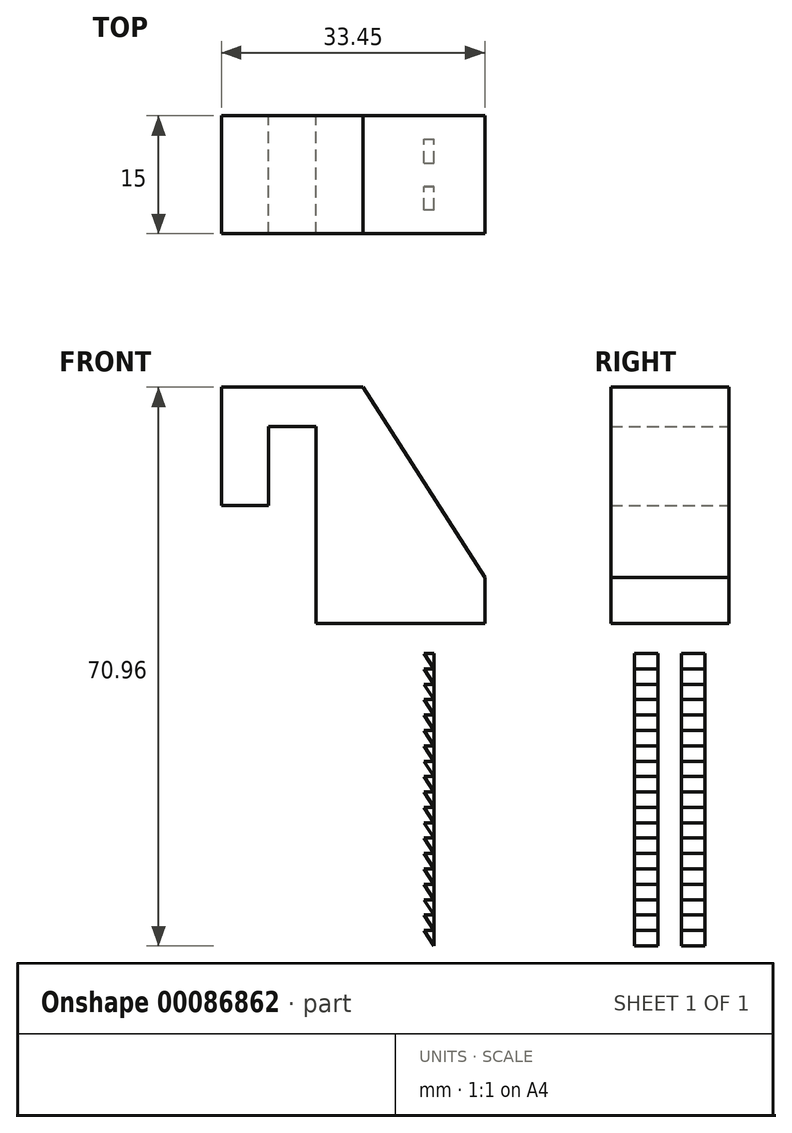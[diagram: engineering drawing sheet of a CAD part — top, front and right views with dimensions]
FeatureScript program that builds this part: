
annotation { "Feature Type Name" : "Feature", "Feature Type Description" : "" }
export const myFeature = defineFeature(function(context is Context, id is Id, definition is map)
    precondition{}
    {
        {
            var Q0;
            Q0=qCreatedBy(makeId("Front.planeOp"),FACE);
            var sketch = newSketch(context, id + "F0", { "sketchPlane" : qUnion([Q0])});
            skLineSegment(sketch, "E0.bottom", {"start": v(-22.95, -4.4) * mm, "end": v(-16.95, -4.4) * mm});
            skLineSegment(sketch, "E0.top", {"start": v(-22.95, 10.6) * mm, "end": v(-16.95, 10.6) * mm});
            skLineSegment(sketch, "E0.left", {"start": v(-22.95, -4.4) * mm, "end": v(-22.95, 10.6) * mm});
            skLineSegment(sketch, "E0.right", {"start": v(-16.95, -4.4) * mm, "end": v(-16.95, 10.6) * mm});
            skLineSegment(sketch, "E1.bottom", {"start": v(-16.95, 10.6) * mm, "end": v(-10.95, 10.6) * mm});
            skLineSegment(sketch, "E1.top", {"start": v(-16.95, 5.6) * mm, "end": v(-10.95, 5.6) * mm});
            skLineSegment(sketch, "E1.left", {"start": v(-16.95, 10.6) * mm, "end": v(-16.95, 5.6) * mm});
            skLineSegment(sketch, "E1.right", {"start": v(-10.95, 10.6) * mm, "end": v(-10.95, 5.6) * mm});
            skLineSegment(sketch, "E2.bottom", {"start": v(-10.95, 10.6) * mm, "end": v(-4.95, 10.6) * mm});
            skLineSegment(sketch, "E2.top", {"start": v(-10.95, -19.4) * mm, "end": v(-4.95, -19.4) * mm});
            skLineSegment(sketch, "E2.left", {"start": v(-10.95, 10.6) * mm, "end": v(-10.95, -19.4) * mm});
            skLineSegment(sketch, "E2.right", {"start": v(-4.95, 10.6) * mm, "end": v(-4.95, -19.4) * mm});
            skLineSegment(sketch, "E3.left", {"start": v(-4.95, -19.4) * mm, "end": v(-4.95, -13.53) * mm});
            skLineSegment(sketch, "E4.bottom", {"start": v(-4.95, -13.53) * mm, "end": v(10.5, -13.53) * mm});
            skLineSegment(sketch, "E4.top", {"start": v(-4.95, -19.4) * mm, "end": v(10.5, -19.4) * mm});
            skLineSegment(sketch, "E4.left", {"start": v(-4.95, -13.53) * mm, "end": v(-4.95, -19.4) * mm});
            skLineSegment(sketch, "E4.right", {"start": v(10.5, -13.53) * mm, "end": v(10.5, -19.4) * mm});
            skLineSegment(sketch, "E5.bottom", {"start": v(10.5, -19.4) * mm, "end": v(4.05, -19.4) * mm});
            skLineSegment(sketch, "E5.top", {"start": v(10.5, -70.16) * mm, "end": v(4.05, -70.16) * mm});
            skLineSegment(sketch, "E5.left", {"start": v(10.5, -19.4) * mm, "end": v(10.5, -70.16) * mm});
            skLineSegment(sketch, "E5.right", {"start": v(4.05, -19.4) * mm, "end": v(4.05, -70.16) * mm});
            skLineSegment(sketch, "E6", {"start": v(4.05, -23.23) * mm, "end": v(2.78, -23.23) * mm});
            skPoint(sketch, "E6.endSnap0", {"position": v(2.78, -19.4) * mm});
            skLineSegment(sketch, "E7", {"start": v(2.78, -23.23) * mm, "end": v(4.05, -25.18) * mm});
            skLineSegment(sketch, "E8", {"start": v(4.05, -25.17) * mm, "end": v(2.78, -25.17) * mm});
            skLineSegment(sketch, "E9", {"start": v(2.78, -25.17) * mm, "end": v(4.05, -27.13) * mm});
            skLineSegment(sketch, "E10", {"start": v(4.05, -27.13) * mm, "end": v(2.78, -27.13) * mm});
            skLineSegment(sketch, "E11", {"start": v(2.78, -27.13) * mm, "end": v(4.05, -29.08) * mm});
            skLineSegment(sketch, "E12", {"start": v(4.05, -29.08) * mm, "end": v(2.78, -29.08) * mm});
            skLineSegment(sketch, "E13", {"start": v(2.78, -29.08) * mm, "end": v(4.05, -31.04) * mm});
            skLineSegment(sketch, "E14", {"start": v(4.05, -31.04) * mm, "end": v(2.78, -31.04) * mm});
            skLineSegment(sketch, "E15", {"start": v(2.78, -31.04) * mm, "end": v(4.05, -33) * mm});
            skLineSegment(sketch, "E16", {"start": v(4.05, -33) * mm, "end": v(2.78, -33) * mm});
            skLineSegment(sketch, "E17", {"start": v(2.78, -33) * mm, "end": v(4.05, -34.95) * mm});
            skLineSegment(sketch, "E18", {"start": v(4.05, -34.95) * mm, "end": v(2.78, -34.95) * mm});
            skLineSegment(sketch, "E19", {"start": v(2.78, -34.95) * mm, "end": v(4.05, -36.9) * mm});
            skLineSegment(sketch, "E20", {"start": v(4.05, -36.9) * mm, "end": v(2.78, -36.9) * mm});
            skLineSegment(sketch, "E21", {"start": v(2.78, -36.9) * mm, "end": v(4.05, -38.86) * mm});
            skLineSegment(sketch, "E22", {"start": v(4.05, -38.86) * mm, "end": v(2.78, -38.86) * mm});
            skLineSegment(sketch, "E23", {"start": v(2.78, -38.86) * mm, "end": v(4.05, -40.81) * mm});
            skLineSegment(sketch, "E24", {"start": v(4.05, -40.81) * mm, "end": v(2.78, -40.81) * mm});
            skLineSegment(sketch, "E25", {"start": v(2.78, -40.81) * mm, "end": v(4.05, -42.77) * mm});
            skLineSegment(sketch, "E26", {"start": v(4.05, -42.77) * mm, "end": v(2.78, -42.77) * mm});
            skLineSegment(sketch, "E27", {"start": v(2.78, -42.77) * mm, "end": v(4.05, -44.72) * mm});
            skLineSegment(sketch, "E28", {"start": v(4.05, -44.72) * mm, "end": v(2.78, -44.72) * mm});
            skLineSegment(sketch, "E29", {"start": v(2.78, -44.72) * mm, "end": v(4.05, -46.67) * mm});
            skLineSegment(sketch, "E30", {"start": v(4.05, -46.67) * mm, "end": v(2.78, -46.67) * mm});
            skLineSegment(sketch, "E31", {"start": v(2.78, -46.67) * mm, "end": v(4.05, -48.63) * mm});
            skLineSegment(sketch, "E32", {"start": v(4.05, -48.63) * mm, "end": v(2.78, -48.63) * mm});
            skLineSegment(sketch, "E33", {"start": v(2.78, -48.63) * mm, "end": v(4.05, -50.58) * mm});
            skLineSegment(sketch, "E34", {"start": v(4.05, -50.58) * mm, "end": v(2.78, -50.58) * mm});
            skLineSegment(sketch, "E35", {"start": v(2.78, -50.58) * mm, "end": v(4.05, -52.54) * mm});
            skLineSegment(sketch, "E36", {"start": v(4.05, -52.54) * mm, "end": v(2.78, -52.54) * mm});
            skLineSegment(sketch, "E37", {"start": v(2.78, -52.54) * mm, "end": v(4.05, -54.5) * mm});
            skLineSegment(sketch, "E38", {"start": v(4.05, -54.5) * mm, "end": v(2.78, -54.5) * mm});
            skLineSegment(sketch, "E39", {"start": v(2.78, -54.5) * mm, "end": v(4.05, -56.45) * mm});
            skLineSegment(sketch, "E40", {"start": v(4.05, -56.45) * mm, "end": v(2.78, -56.45) * mm});
            skLineSegment(sketch, "E41", {"start": v(2.78, -56.45) * mm, "end": v(4.05, -58.4) * mm});
            skLineSegment(sketch, "E42", {"start": v(4.05, -58.4) * mm, "end": v(2.78, -58.4) * mm});
            skLineSegment(sketch, "E43", {"start": v(2.78, -58.4) * mm, "end": v(4.05, -60.36) * mm});
            skLineSegment(sketch, "E44", {"start": v(4.05, -60.36) * mm, "end": v(2.78, -60.36) * mm});
            skLineSegment(sketch, "E45", {"start": v(2.78, -60.36) * mm, "end": v(4.05, -62.31) * mm});
            skLineSegment(sketch, "E46", {"start": v(4.05, -62.31) * mm, "end": v(2.78, -62.31) * mm});
            skLineSegment(sketch, "E47", {"start": v(2.78, -62.31) * mm, "end": v(4.05, -64.27) * mm});
            skLineSegment(sketch, "E48", {"start": v(4.05, -64.27) * mm, "end": v(2.78, -64.27) * mm});
            skLineSegment(sketch, "E49", {"start": v(2.78, -64.27) * mm, "end": v(4.05, -66.22) * mm});
            skLineSegment(sketch, "E50", {"start": v(4.05, -66.22) * mm, "end": v(2.78, -66.22) * mm});
            skLineSegment(sketch, "E51", {"start": v(2.78, -66.22) * mm, "end": v(4.05, -68.18) * mm});
            skLineSegment(sketch, "E52", {"start": v(4.05, -68.18) * mm, "end": v(2.78, -68.18) * mm});
            skLineSegment(sketch, "E53", {"start": v(2.78, -68.18) * mm, "end": v(4.05, -70.13) * mm});
            skLineSegment(sketch, "E54", {"start": v(10.5, -13.53) * mm, "end": v(-4.95, 10.6) * mm});
            skLineSegment(sketch, "E55", {"start": v(10.5, -70.16) * mm, "end": v(4.05, -60.36) * mm});
            skLineSegment(sketch, "E56", {"start": v(9.74, -69) * mm, "end": v(10.5, -69) * mm});
            skSolve(sketch);
        }
        {
            var Q0;
            Q0=makeQuery(id+"F0.imprint","IMPRINT",FACE,{"disambiguationData":[TD([[makeQuery(id+"F0.imprint","IMPRINT",EDGE,{"derivedFrom":sQuery(id+"F0.wireOp",EDGE,"E0.bottom")}),1.0]])]});
            var Q1;
            {var subQ0=sQuery(id+"F0.wireOp",EDGE,"E10");Q1=makeQuery(id+"F0.imprint","IMPRINT",FACE,{"disambiguationData":[TD([[makeQuery(id+"F0.imprint","IMPRINT",EDGE,{"derivedFrom":subQ0}),1.0]])]});}
            var Q2;
            {var subQ0=sQuery(id+"F0.wireOp",EDGE,"E12");Q2=makeQuery(id+"F0.imprint","IMPRINT",FACE,{"disambiguationData":[TD([[makeQuery(id+"F0.imprint","IMPRINT",EDGE,{"derivedFrom":subQ0}),1.0]])]});}
            var Q3;
            {var subQ0=sQuery(id+"F0.wireOp",EDGE,"E14");Q3=makeQuery(id+"F0.imprint","IMPRINT",FACE,{"disambiguationData":[TD([[makeQuery(id+"F0.imprint","IMPRINT",EDGE,{"derivedFrom":subQ0}),1.0]])]});}
            var Q4;
            {var subQ0=sQuery(id+"F0.wireOp",EDGE,"E16");Q4=makeQuery(id+"F0.imprint","IMPRINT",FACE,{"disambiguationData":[TD([[makeQuery(id+"F0.imprint","IMPRINT",EDGE,{"derivedFrom":subQ0}),1.0]])]});}
            var Q5;
            {var subQ0=sQuery(id+"F0.wireOp",EDGE,"E18");Q5=makeQuery(id+"F0.imprint","IMPRINT",FACE,{"disambiguationData":[TD([[makeQuery(id+"F0.imprint","IMPRINT",EDGE,{"derivedFrom":subQ0}),1.0]])]});}
            var Q6;
            {var subQ0=sQuery(id+"F0.wireOp",EDGE,"E20");Q6=makeQuery(id+"F0.imprint","IMPRINT",FACE,{"disambiguationData":[TD([[makeQuery(id+"F0.imprint","IMPRINT",EDGE,{"derivedFrom":subQ0}),1.0]])]});}
            var Q7;
            {var subQ0=sQuery(id+"F0.wireOp",EDGE,"E22");Q7=makeQuery(id+"F0.imprint","IMPRINT",FACE,{"disambiguationData":[TD([[makeQuery(id+"F0.imprint","IMPRINT",EDGE,{"derivedFrom":subQ0}),1.0]])]});}
            var Q8;
            {var subQ0=sQuery(id+"F0.wireOp",EDGE,"E24");Q8=makeQuery(id+"F0.imprint","IMPRINT",FACE,{"disambiguationData":[TD([[makeQuery(id+"F0.imprint","IMPRINT",EDGE,{"derivedFrom":subQ0}),1.0]])]});}
            var Q9;
            {var subQ0=sQuery(id+"F0.wireOp",EDGE,"E26");Q9=makeQuery(id+"F0.imprint","IMPRINT",FACE,{"disambiguationData":[TD([[makeQuery(id+"F0.imprint","IMPRINT",EDGE,{"derivedFrom":subQ0}),1.0]])]});}
            var Q10;
            {var subQ0=sQuery(id+"F0.wireOp",EDGE,"E28");Q10=makeQuery(id+"F0.imprint","IMPRINT",FACE,{"disambiguationData":[TD([[makeQuery(id+"F0.imprint","IMPRINT",EDGE,{"derivedFrom":subQ0}),1.0]])]});}
            var Q11;
            {var subQ0=sQuery(id+"F0.wireOp",EDGE,"E30");Q11=makeQuery(id+"F0.imprint","IMPRINT",FACE,{"disambiguationData":[TD([[makeQuery(id+"F0.imprint","IMPRINT",EDGE,{"derivedFrom":subQ0}),1.0]])]});}
            var Q12;
            {var subQ0=sQuery(id+"F0.wireOp",EDGE,"E32");Q12=makeQuery(id+"F0.imprint","IMPRINT",FACE,{"disambiguationData":[TD([[makeQuery(id+"F0.imprint","IMPRINT",EDGE,{"derivedFrom":subQ0}),1.0]])]});}
            var Q13;
            {var subQ0=sQuery(id+"F0.wireOp",EDGE,"E34");Q13=makeQuery(id+"F0.imprint","IMPRINT",FACE,{"disambiguationData":[TD([[makeQuery(id+"F0.imprint","IMPRINT",EDGE,{"derivedFrom":subQ0}),1.0]])]});}
            var Q14;
            {var subQ0=sQuery(id+"F0.wireOp",EDGE,"E36");Q14=makeQuery(id+"F0.imprint","IMPRINT",FACE,{"disambiguationData":[TD([[makeQuery(id+"F0.imprint","IMPRINT",EDGE,{"derivedFrom":subQ0}),1.0]])]});}
            var Q15;
            {var subQ0=sQuery(id+"F0.wireOp",EDGE,"E38");Q15=makeQuery(id+"F0.imprint","IMPRINT",FACE,{"disambiguationData":[TD([[makeQuery(id+"F0.imprint","IMPRINT",EDGE,{"derivedFrom":subQ0}),1.0]])]});}
            var Q16;
            {var subQ0=sQuery(id+"F0.wireOp",EDGE,"E40");Q16=makeQuery(id+"F0.imprint","IMPRINT",FACE,{"disambiguationData":[TD([[makeQuery(id+"F0.imprint","IMPRINT",EDGE,{"derivedFrom":subQ0}),1.0]])]});}
            var Q17;
            {var subQ0=sQuery(id+"F0.wireOp",EDGE,"E42");Q17=makeQuery(id+"F0.imprint","IMPRINT",FACE,{"disambiguationData":[TD([[makeQuery(id+"F0.imprint","IMPRINT",EDGE,{"derivedFrom":subQ0}),1.0]])]});}
            var Q18;
            {var subQ0=sQuery(id+"F0.wireOp",EDGE,"E1.bottom");Q18=makeQuery(id+"F0.imprint","IMPRINT",FACE,{"disambiguationData":[TD([[makeQuery(id+"F0.imprint","IMPRINT",EDGE,{"derivedFrom":subQ0}),-1.0]])]});}
            var Q19;
            Q19=makeQuery(id+"F0.imprint","IMPRINT",FACE,{"disambiguationData":[TD([[makeQuery(id+"F0.imprint","IMPRINT",EDGE,{"derivedFrom":sQuery(id+"F0.wireOp",EDGE,"E2.right")}),1.0]])]});
            var Q20;
            {var subQ0=sQuery(id+"F0.wireOp",EDGE,"E6");Q20=makeQuery(id+"F0.imprint","IMPRINT",FACE,{"disambiguationData":[TD([[makeQuery(id+"F0.imprint","IMPRINT",EDGE,{"derivedFrom":subQ0}),1.0]])]});}
            var Q21;
            {var subQ3=sQuery(id+"F0.wireOp",EDGE,"E9");Q21=makeQuery(id+"F0.imprint","IMPRINT",FACE,{"disambiguationData":[TD([[makeQuery(id+"F0.imprint","IMPRINT",EDGE,{"derivedFrom":subQ3}),1.0]])]});}
            var Q22;
            {var subQ3=sQuery(id+"F0.wireOp",EDGE,"E2.bottom");Q22=makeQuery(id+"F0.imprint","IMPRINT",FACE,{"disambiguationData":[TD([[makeQuery(id+"F0.imprint","IMPRINT",EDGE,{"derivedFrom":subQ3}),-1.0]])]});}
            var Q23;
            Q23=makeQuery(id+"F0.imprint","IMPRINT",FACE,{"disambiguationData":[TD([[makeQuery(id+"F0.imprint","IMPRINT",EDGE,{"derivedFrom":sQuery(id+"F0.wireOp",EDGE,"E4.bottom")}),-1.0]])]});
            var Q24;
            {var subQ0=sQuery(id+"F0.wireOp",EDGE,"E7");var subQ1=sQuery(id+"F0.wireOp",EDGE,"E5.right");var subQ2=makeQuery(id+"F0.imprint","INTERSECT",VERTEX,{"derivedFrom":[subQ1,subQ0]});Q24=makeQuery(id+"F0.imprint","IMPRINT",FACE,{"disambiguationData":[TD([[makeQuery(id+"F0.imprint","IMPRINT",EDGE,{"disambiguationData":[TD([[subQ2,1.0]])],"derivedFrom":subQ1}),-1.0]])]});}
            var Q25;
            {var subQ15=sQuery(id+"F0.wireOp",EDGE,"E5.bottom");Q25=makeQuery(id+"F0.imprint","IMPRINT",FACE,{"disambiguationData":[TD([[makeQuery(id+"F0.imprint","IMPRINT",EDGE,{"derivedFrom":subQ15}),1.0]])]});}
            extrude(context, id + "F1", {"entities" : qUnion([Q0, Q1, Q2, Q3, Q4, Q5, Q6, Q7, Q8, Q9, Q10, Q11, Q12, Q13, Q14, Q15, Q16, Q17, Q18, Q19, Q20, Q21, Q22, Q23, Q24, Q25]), "depth" : 15 * mm});
        }
        {
            var Q0;
            Q0=makeQuery(id+"F1.opExtrude","CAP_FACE",FACE,{"disambiguationData":[OSD([sQuery(id+"F0.wireOp",EDGE,"E0.bottom"),sQuery(id+"F0.wireOp",EDGE,"E0.top"),sQuery(id+"F0.wireOp",EDGE,"E0.left"),sQuery(id+"F0.wireOp",EDGE,"E0.right"),sQuery(id+"F0.wireOp",EDGE,"E1.bottom"),sQuery(id+"F0.wireOp",EDGE,"E1.top"),sQuery(id+"F0.wireOp",EDGE,"E2.bottom"),sQuery(id+"F0.wireOp",EDGE,"E2.top"),sQuery(id+"F0.wireOp",EDGE,"E2.left"),sQuery(id+"F0.wireOp",EDGE,"E2.right"),sQuery(id+"F0.wireOp",EDGE,"E4.bottom"),sQuery(id+"F0.wireOp",EDGE,"E4.top"),sQuery(id+"F0.wireOp",EDGE,"E4.right"),sQuery(id+"F0.wireOp",EDGE,"E5.top"),sQuery(id+"F0.wireOp",EDGE,"E5.left"),sQuery(id+"F0.wireOp",EDGE,"E5.right"),sQuery(id+"F0.wireOp",EDGE,"E6"),sQuery(id+"F0.wireOp",EDGE,"E7"),sQuery(id+"F0.wireOp",EDGE,"E8"),sQuery(id+"F0.wireOp",EDGE,"E9"),sQuery(id+"F0.wireOp",EDGE,"E10"),sQuery(id+"F0.wireOp",EDGE,"E11"),sQuery(id+"F0.wireOp",EDGE,"E12"),sQuery(id+"F0.wireOp",EDGE,"E13"),sQuery(id+"F0.wireOp",EDGE,"E14"),sQuery(id+"F0.wireOp",EDGE,"E15"),sQuery(id+"F0.wireOp",EDGE,"E16"),sQuery(id+"F0.wireOp",EDGE,"E17"),sQuery(id+"F0.wireOp",EDGE,"E18"),sQuery(id+"F0.wireOp",EDGE,"E19"),sQuery(id+"F0.wireOp",EDGE,"E20"),sQuery(id+"F0.wireOp",EDGE,"E21"),sQuery(id+"F0.wireOp",EDGE,"E22"),sQuery(id+"F0.wireOp",EDGE,"E23"),sQuery(id+"F0.wireOp",EDGE,"E24"),sQuery(id+"F0.wireOp",EDGE,"E25"),sQuery(id+"F0.wireOp",EDGE,"E26"),sQuery(id+"F0.wireOp",EDGE,"E27"),sQuery(id+"F0.wireOp",EDGE,"E28"),sQuery(id+"F0.wireOp",EDGE,"E29"),sQuery(id+"F0.wireOp",EDGE,"E30"),sQuery(id+"F0.wireOp",EDGE,"E31"),sQuery(id+"F0.wireOp",EDGE,"E32"),sQuery(id+"F0.wireOp",EDGE,"E33"),sQuery(id+"F0.wireOp",EDGE,"E34"),sQuery(id+"F0.wireOp",EDGE,"E35"),sQuery(id+"F0.wireOp",EDGE,"E36"),sQuery(id+"F0.wireOp",EDGE,"E37"),sQuery(id+"F0.wireOp",EDGE,"E38"),sQuery(id+"F0.wireOp",EDGE,"E39"),sQuery(id+"F0.wireOp",EDGE,"E40"),sQuery(id+"F0.wireOp",EDGE,"E41"),sQuery(id+"F0.wireOp",EDGE,"E42"),sQuery(id+"F0.wireOp",EDGE,"E43"),sQuery(id+"F0.wireOp",EDGE,"E44"),sQuery(id+"F0.wireOp",EDGE,"E45"),sQuery(id+"F0.wireOp",EDGE,"E46"),sQuery(id+"F0.wireOp",EDGE,"E47"),sQuery(id+"F0.wireOp",EDGE,"E48"),sQuery(id+"F0.wireOp",EDGE,"E49"),sQuery(id+"F0.wireOp",EDGE,"E50"),sQuery(id+"F0.wireOp",EDGE,"E51"),sQuery(id+"F0.wireOp",EDGE,"E52"),sQuery(id+"F0.wireOp",EDGE,"E53")])],"isStart":true});
            var sketch = newSketch(context, id + "F2", { "sketchPlane" : qUnion([Q0])});
            skLineSegment(sketch, "E57.bottom", {"start": v(-10.5, -19.4) * mm, "end": v(0, -19.4) * mm});
            skLineSegment(sketch, "E57.top", {"start": v(-10.5, -70.72) * mm, "end": v(0, -70.72) * mm});
            skLineSegment(sketch, "E57.left", {"start": v(-10.5, -19.4) * mm, "end": v(-10.5, -70.72) * mm});
            skLineSegment(sketch, "E57.right", {"start": v(0, -19.4) * mm, "end": v(0, -70.72) * mm});
            skSolve(sketch);
        }
        {
            var Q0;
            Q0 = qSketchRegion(id + "F2", true);
            extrude(context, id + "F3", {"entities" : qUnion([Q0]), "operationType" : NewBodyOperationType.REMOVE, "oppositeDirection" : true, "depth" : 3 * mm});
        }
        {
            var Q0;
            Q0=makeQuery(id+"F1.opExtrude","CAP_FACE",FACE,{"disambiguationData":[OSD([sQuery(id+"F0.wireOp",EDGE,"E0.bottom"),sQuery(id+"F0.wireOp",EDGE,"E0.top"),sQuery(id+"F0.wireOp",EDGE,"E0.left"),sQuery(id+"F0.wireOp",EDGE,"E0.right"),sQuery(id+"F0.wireOp",EDGE,"E1.bottom"),sQuery(id+"F0.wireOp",EDGE,"E1.top"),sQuery(id+"F0.wireOp",EDGE,"E2.bottom"),sQuery(id+"F0.wireOp",EDGE,"E2.top"),sQuery(id+"F0.wireOp",EDGE,"E2.left"),sQuery(id+"F0.wireOp",EDGE,"E2.right"),sQuery(id+"F0.wireOp",EDGE,"E4.bottom"),sQuery(id+"F0.wireOp",EDGE,"E4.top"),sQuery(id+"F0.wireOp",EDGE,"E4.right"),sQuery(id+"F0.wireOp",EDGE,"E5.top"),sQuery(id+"F0.wireOp",EDGE,"E5.left"),sQuery(id+"F0.wireOp",EDGE,"E5.right"),sQuery(id+"F0.wireOp",EDGE,"E6"),sQuery(id+"F0.wireOp",EDGE,"E7"),sQuery(id+"F0.wireOp",EDGE,"E8"),sQuery(id+"F0.wireOp",EDGE,"E9"),sQuery(id+"F0.wireOp",EDGE,"E10"),sQuery(id+"F0.wireOp",EDGE,"E11"),sQuery(id+"F0.wireOp",EDGE,"E12"),sQuery(id+"F0.wireOp",EDGE,"E13"),sQuery(id+"F0.wireOp",EDGE,"E14"),sQuery(id+"F0.wireOp",EDGE,"E15"),sQuery(id+"F0.wireOp",EDGE,"E16"),sQuery(id+"F0.wireOp",EDGE,"E17"),sQuery(id+"F0.wireOp",EDGE,"E18"),sQuery(id+"F0.wireOp",EDGE,"E19"),sQuery(id+"F0.wireOp",EDGE,"E20"),sQuery(id+"F0.wireOp",EDGE,"E21"),sQuery(id+"F0.wireOp",EDGE,"E22"),sQuery(id+"F0.wireOp",EDGE,"E23"),sQuery(id+"F0.wireOp",EDGE,"E24"),sQuery(id+"F0.wireOp",EDGE,"E25"),sQuery(id+"F0.wireOp",EDGE,"E26"),sQuery(id+"F0.wireOp",EDGE,"E27"),sQuery(id+"F0.wireOp",EDGE,"E28"),sQuery(id+"F0.wireOp",EDGE,"E29"),sQuery(id+"F0.wireOp",EDGE,"E30"),sQuery(id+"F0.wireOp",EDGE,"E31"),sQuery(id+"F0.wireOp",EDGE,"E32"),sQuery(id+"F0.wireOp",EDGE,"E33"),sQuery(id+"F0.wireOp",EDGE,"E34"),sQuery(id+"F0.wireOp",EDGE,"E35"),sQuery(id+"F0.wireOp",EDGE,"E36"),sQuery(id+"F0.wireOp",EDGE,"E37"),sQuery(id+"F0.wireOp",EDGE,"E38"),sQuery(id+"F0.wireOp",EDGE,"E39"),sQuery(id+"F0.wireOp",EDGE,"E40"),sQuery(id+"F0.wireOp",EDGE,"E41"),sQuery(id+"F0.wireOp",EDGE,"E42"),sQuery(id+"F0.wireOp",EDGE,"E43"),sQuery(id+"F0.wireOp",EDGE,"E44"),sQuery(id+"F0.wireOp",EDGE,"E45"),sQuery(id+"F0.wireOp",EDGE,"E46"),sQuery(id+"F0.wireOp",EDGE,"E47"),sQuery(id+"F0.wireOp",EDGE,"E48"),sQuery(id+"F0.wireOp",EDGE,"E49"),sQuery(id+"F0.wireOp",EDGE,"E50"),sQuery(id+"F0.wireOp",EDGE,"E51"),sQuery(id+"F0.wireOp",EDGE,"E52"),sQuery(id+"F0.wireOp",EDGE,"E53")])],"isStart":false});
            var sketch = newSketch(context, id + "F4", { "sketchPlane" : qUnion([Q0])});
            skLineSegment(sketch, "E58.bottom", {"start": v(10.5, -19.4) * mm, "end": v(0, -19.4) * mm});
            skLineSegment(sketch, "E58.top", {"start": v(10.5, -71.7) * mm, "end": v(0, -71.7) * mm});
            skLineSegment(sketch, "E58.left", {"start": v(10.5, -19.4) * mm, "end": v(10.5, -71.7) * mm});
            skLineSegment(sketch, "E58.right", {"start": v(0, -19.4) * mm, "end": v(0, -71.7) * mm});
            skSolve(sketch);
        }
        {
            var Q0;
            Q0 = qSketchRegion(id + "F4", true);
            extrude(context, id + "F5", {"entities" : qUnion([Q0]), "operationType" : NewBodyOperationType.REMOVE, "oppositeDirection" : true, "depth" : 3 * mm});
        }
        {
            var Q0;
            Q0=makeQuery(id+"F1.opExtrude","SWEPT_FACE",FACE,{"disambiguationData":[OSD([sQuery(id+"F0.wireOp",EDGE,"E4.right"),sQuery(id+"F0.wireOp",EDGE,"E5.left")])]});
            var sketch = newSketch(context, id + "F6", { "sketchPlane" : qUnion([Q0])});
            skLineSegment(sketch, "E59.bottom", {"start": v(-6, -69) * mm, "end": v(-9, -69) * mm});
            skLineSegment(sketch, "E59.top", {"start": v(-6, -19.4) * mm, "end": v(-9, -19.4) * mm});
            skLineSegment(sketch, "E59.left", {"start": v(-6, -69) * mm, "end": v(-6, -19.4) * mm});
            skLineSegment(sketch, "E59.right", {"start": v(-9, -69) * mm, "end": v(-9, -19.4) * mm});
            skSolve(sketch);
        }
        {
            var Q0;
            Q0 = qSketchRegion(id + "F6", true);
            extrude(context, id + "F7", {"entities" : qUnion([Q0]), "operationType" : NewBodyOperationType.REMOVE, "oppositeDirection" : true, "depth" : 25.4 * mm});
        }
    });
